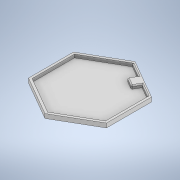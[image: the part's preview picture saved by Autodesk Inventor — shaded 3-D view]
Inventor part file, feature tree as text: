
AUTODESK INVENTOR PART (.ipt)
format: ipt  version: 2020 (Build 240168000, 168)  size: 144,896 bytes
history: native  units: in
note: dims shown in document units (in); Inventor stores cm internally (conversion verified against a paired STEP export)
features: extrude x3, sketch x3, fillet x2
ambient origin geometry x8: Origin, YZ Plane, XZ Plane, XY Plane, X Axis, Y Axis, Z Axis, Center Point
bodies: Solid1 (feature_tree)
feature tree (8):
  extrude  "Extrusion1"  Depth=3.3465in
  extrude  "Extrusion2"  TaperAngle=0.0deg  [1 undecoded]
  extrude  "Extrusion3"  Depth=0.2362in TaperAngle=0.0deg
  fillet  "Fillet1"  [1 undecoded]
  fillet  "Fillet2"  Radius=1.2795in
  sketch  "Sketch1"  dims[d1=0.0in d2=3.3465in]
  sketch  "Sketch2"  dims[d3=0.315in d4=0.0in d5=0.0in]
  sketch  "Sketch4"  dims[d6=3.1496in d7=0.2362in d8=0.0in d23=0.0in d25=1.2795in d26=0.7874in d27=0.2362in d28=0.5906in d29=0.0in d30=0.0787in d31=0.0787in]
note: 2 required parameter values undecoded (feature->parameter linkage not recoverable at this tier; creation-order binding heuristic only, values carry confidence <= 0.55)
